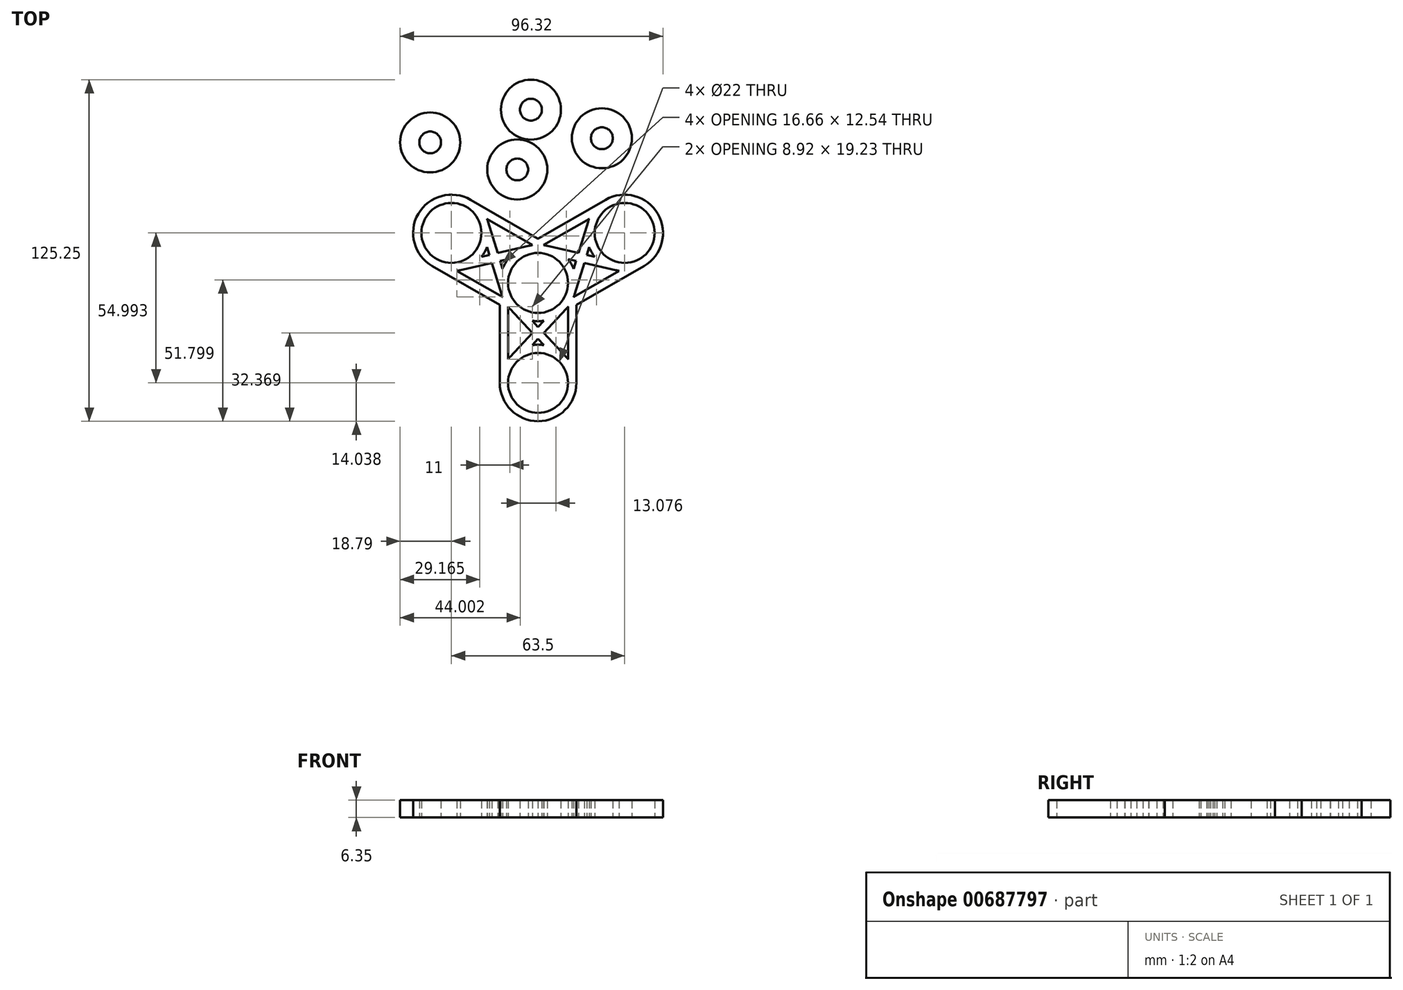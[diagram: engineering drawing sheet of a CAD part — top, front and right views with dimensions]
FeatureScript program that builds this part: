
annotation { "Feature Type Name" : "Feature", "Feature Type Description" : "" }
export const myFeature = defineFeature(function(context is Context, id is Id, definition is map)
    precondition{}
    {
        {
            var Q0;
            Q0=qCreatedBy(makeId("Top.planeOp"),FACE);
            var sketch = newSketch(context, id + "F0", { "sketchPlane" : qUnion([Q0])});
            skCircle(sketch, "E0", {"center": v(0, 0) * mm, "radius": 11 * mm});
            skCircle(sketch, "E1", {"center": v(0, 0) * mm, "radius": 4 * mm});
            skArc(sketch, "E2", {"start": v(-13.42, -4.09) * mm, "mid": v(-13.25, -4.63) * mm, "end": v(-13.05, -5.17) * mm});
            skCircle(sketch, "E3", {"center": v(31.75, 18.33) * mm, "radius": 11 * mm});
            skCircle(sketch, "E4", {"center": v(31.75, 18.33) * mm, "radius": 4 * mm});
            skArc(sketch, "E5", {"start": v(18.69, 13.2) * mm, "mid": v(19.6, 11.31) * mm, "end": v(20.77, 9.59) * mm});
            skCircle(sketch, "E6", {"center": v(-31.75, 18.33) * mm, "radius": 11 * mm});
            skCircle(sketch, "E7", {"center": v(-31.75, 18.33) * mm, "radius": 4 * mm});
            skArc(sketch, "E8", {"start": v(-18.33, 22.42) * mm, "mid": v(-18.5, 22.96) * mm, "end": v(-18.7, 23.5) * mm});
            skCircle(sketch, "E9", {"center": v(0, -36.66) * mm, "radius": 11 * mm});
            skCircle(sketch, "E10", {"center": v(0, -36.66) * mm, "radius": 4 * mm});
            skArc(sketch, "E11", {"start": v(-10.25, -27.08) * mm, "mid": v(-10.64, -27.5) * mm, "end": v(-11, -27.95) * mm});
            skLineSegment(sketch, "E12", {"start": v(-31.75, 18.33) * mm, "end": v(31.75, 18.33) * mm, "construction": true});
            skLineSegment(sketch, "E13", {"start": v(31.75, 18.33) * mm, "end": v(0, -36.66) * mm, "construction": true});
            skLineSegment(sketch, "E14", {"start": v(-31.75, 18.33) * mm, "end": v(0, -36.66) * mm, "construction": true});
            skLineSegment(sketch, "E15", {"start": v(0, 16.2) * mm, "end": v(24.73, 30.48) * mm});
            skLineSegment(sketch, "E16", {"start": v(-14.03, -8.1) * mm, "end": v(-14.03, -36.66) * mm});
            skLineSegment(sketch, "E17", {"start": v(11, -27.95) * mm, "end": v(11, -8.71) * mm});
            skLineSegment(sketch, "E18", {"start": v(14.03, -8.1) * mm, "end": v(38.77, 6.18) * mm});
            skLineSegment(sketch, "E19", {"start": v(-18.7, 23.5) * mm, "end": v(-2.05, 13.88) * mm});
            skLineSegment(sketch, "E20", {"start": v(14.03, -36.66) * mm, "end": v(14.03, -8.1) * mm});
            skLineSegment(sketch, "E21", {"start": v(-18.33, 22.42) * mm, "end": v(-14.84, 10.96) * mm});
            skLineSegment(sketch, "E22", {"start": v(-28.58, 4.66) * mm, "end": v(-16.91, 7.37) * mm});
            skLineSegment(sketch, "E23.trimOffspring", {"start": v(-13.95, 8.05) * mm, "end": v(-10.98, 8.75) * mm});
            skLineSegment(sketch, "E24.trimOffspring", {"start": v(-16.91, 7.37) * mm, "end": v(-13.42, -4.09) * mm});
            skLineSegment(sketch, "E25.trimOffspring", {"start": v(-13.95, 8.05) * mm, "end": v(-13.06, 5.13) * mm});
            skArc(sketch, "E26.trimOffspring", {"start": v(-20.77, 9.59) * mm, "mid": v(-19.6, 11.31) * mm, "end": v(-18.69, 13.2) * mm});
            skLineSegment(sketch, "E27.trimOffspring", {"start": v(-18.69, 13.2) * mm, "end": v(-17.8, 10.28) * mm});
            skArc(sketch, "E28.trimOffspring", {"start": v(-10.98, 8.75) * mm, "mid": v(-12.15, 7.02) * mm, "end": v(-13.06, 5.13) * mm});
            skArc(sketch, "E29.trimOffspring", {"start": v(-29.7, 4.45) * mm, "mid": v(-29.14, 4.54) * mm, "end": v(-28.58, 4.66) * mm});
            skLineSegment(sketch, "E30.trimOffspring", {"start": v(0, 16.2) * mm, "end": v(-24.73, 30.48) * mm});
            skArc(sketch, "E31.trimOffspring", {"start": v(-2.05, 13.88) * mm, "mid": v(-2.61, 13.79) * mm, "end": v(-3.17, 13.67) * mm});
            skLineSegment(sketch, "E32.trimOffspring", {"start": v(2.05, 13.88) * mm, "end": v(18.7, 23.5) * mm});
            skArc(sketch, "E33.trimOffspring", {"start": v(-11, -8.71) * mm, "mid": v(-10.64, -9.16) * mm, "end": v(-10.25, -9.58) * mm});
            skLineSegment(sketch, "E34.trimOffspring", {"start": v(-13.05, -5.17) * mm, "end": v(-29.7, 4.45) * mm});
            skLineSegment(sketch, "E35.trimOffspring", {"start": v(-11, -8.71) * mm, "end": v(-11, -27.95) * mm});
            skLineSegment(sketch, "E36.trimOffspring", {"start": v(-14.03, -8.1) * mm, "end": v(-38.77, 6.18) * mm});
            skLineSegment(sketch, "E37.trimOffspring", {"start": v(13.05, -5.17) * mm, "end": v(29.7, 4.45) * mm});
            skArc(sketch, "E38.trimOffspring", {"start": v(13.05, -5.17) * mm, "mid": v(13.25, -4.63) * mm, "end": v(13.42, -4.09) * mm});
            skLineSegment(sketch, "E39", {"start": v(13.06, 5.13) * mm, "end": v(13.95, 8.05) * mm});
            skLineSegment(sketch, "E40", {"start": v(3.17, 13.67) * mm, "end": v(14.84, 10.96) * mm});
            skLineSegment(sketch, "E41", {"start": v(10.98, 8.75) * mm, "end": v(13.95, 8.05) * mm});
            skLineSegment(sketch, "E42", {"start": v(10.25, -27.08) * mm, "end": v(2.08, -18.33) * mm});
            skLineSegment(sketch, "E43", {"start": v(-10.25, -27.08) * mm, "end": v(-2.08, -18.33) * mm});
            skLineSegment(sketch, "E44.trimOffspring", {"start": v(-20.77, 9.59) * mm, "end": v(-17.8, 10.28) * mm});
            skLineSegment(sketch, "E45.trimOffspring", {"start": v(-14.84, 10.96) * mm, "end": v(-3.17, 13.67) * mm});
            skArc(sketch, "E46.trimOffspring", {"start": v(-24.73, 30.48) * mm, "mid": v(-43.9, 25.35) * mm, "end": v(-38.77, 6.18) * mm});
            skLineSegment(sketch, "E47.trimOffspring", {"start": v(17.8, 10.28) * mm, "end": v(20.77, 9.59) * mm});
            skLineSegment(sketch, "E48.trimOffspring", {"start": v(16.91, 7.37) * mm, "end": v(28.58, 4.66) * mm});
            skLineSegment(sketch, "E49.trimOffspring", {"start": v(14.84, 10.96) * mm, "end": v(18.33, 22.42) * mm});
            skArc(sketch, "E50.trimOffspring", {"start": v(3.17, 13.67) * mm, "mid": v(2.61, 13.79) * mm, "end": v(2.05, 13.88) * mm});
            skArc(sketch, "E51.trimOffspring", {"start": v(13.06, 5.13) * mm, "mid": v(12.15, 7.02) * mm, "end": v(10.98, 8.75) * mm});
            skLineSegment(sketch, "E52.trimOffspring", {"start": v(16.91, 7.37) * mm, "end": v(13.42, -4.09) * mm});
            skLineSegment(sketch, "E53.trimOffspring", {"start": v(18.69, 13.2) * mm, "end": v(17.8, 10.28) * mm});
            skArc(sketch, "E54.trimOffspring", {"start": v(28.58, 4.66) * mm, "mid": v(29.14, 4.54) * mm, "end": v(29.7, 4.45) * mm});
            skArc(sketch, "E55.trimOffspring", {"start": v(38.77, 6.18) * mm, "mid": v(43.9, 25.35) * mm, "end": v(24.73, 30.48) * mm});
            skArc(sketch, "E56.trimOffspring", {"start": v(18.7, 23.5) * mm, "mid": v(18.5, 22.96) * mm, "end": v(18.33, 22.42) * mm});
            skArc(sketch, "E57.trimOffspring", {"start": v(-2.09, -13.88) * mm, "mid": v(0, -14.03) * mm, "end": v(2.09, -13.88) * mm});
            skArc(sketch, "E58.trimOffspring", {"start": v(10.25, -9.58) * mm, "mid": v(10.64, -9.16) * mm, "end": v(11, -8.71) * mm});
            skLineSegment(sketch, "E59.trimOffspring", {"start": v(0, -16.1) * mm, "end": v(2.09, -13.88) * mm});
            skLineSegment(sketch, "E60.trimOffspring", {"start": v(0, -16.1) * mm, "end": v(-2.09, -13.88) * mm});
            skLineSegment(sketch, "E61.trimOffspring", {"start": v(2.08, -18.33) * mm, "end": v(10.25, -9.58) * mm});
            skLineSegment(sketch, "E62.trimOffspring", {"start": v(-2.08, -18.33) * mm, "end": v(-10.25, -9.58) * mm});
            skLineSegment(sketch, "E63.trimOffspring", {"start": v(-2.09, -22.78) * mm, "end": v(0, -20.55) * mm});
            skLineSegment(sketch, "E64.trimOffspring", {"start": v(2.09, -22.78) * mm, "end": v(0, -20.55) * mm});
            skArc(sketch, "E65.trimOffspring", {"start": v(2.09, -22.78) * mm, "mid": v(0, -22.63) * mm, "end": v(-2.09, -22.78) * mm});
            skArc(sketch, "E66.trimOffspring", {"start": v(11, -27.95) * mm, "mid": v(10.64, -27.5) * mm, "end": v(10.25, -27.08) * mm});
            skArc(sketch, "E67.trimOffspring", {"start": v(-14.03, -36.66) * mm, "mid": v(0, -50.7) * mm, "end": v(14.03, -36.66) * mm});
            skLineSegment(sketch, "E68", {"start": v(31.75, 18.33) * mm, "end": v(0, 0) * mm, "construction": true});
            skLineSegment(sketch, "E69", {"start": v(-31.75, 18.33) * mm, "end": v(0, 0) * mm, "construction": true});
            skLineSegment(sketch, "E70", {"start": v(0, -36.66) * mm, "end": v(0, 0) * mm, "construction": true});
            skCircle(sketch, "E71", {"center": v(-39.54, 51.54) * mm, "radius": 11 * mm});
            skCircle(sketch, "E72", {"center": v(-39.54, 51.54) * mm, "radius": 4 * mm});
            skCircle(sketch, "E73", {"center": v(-7.62, 41.62) * mm, "radius": 11 * mm});
            skCircle(sketch, "E74", {"center": v(-7.62, 41.62) * mm, "radius": 4 * mm});
            skCircle(sketch, "E75", {"center": v(-2.62, 63.55) * mm, "radius": 11 * mm});
            skCircle(sketch, "E76", {"center": v(-2.62, 63.55) * mm, "radius": 4 * mm});
            skCircle(sketch, "E77", {"center": v(23.39, 53.08) * mm, "radius": 11 * mm});
            skCircle(sketch, "E78", {"center": v(23.39, 53.08) * mm, "radius": 4 * mm});
            skSolve(sketch);
        }
        {
            var Q0;
            Q0 = qSketchRegion(id + "F0", true);
            extrude(context, id + "F1", {"entities" : qUnion([Q0]), "depth" : 6.35 * mm, "offsetDistance" : 25.4 * mm});
        }
    });
